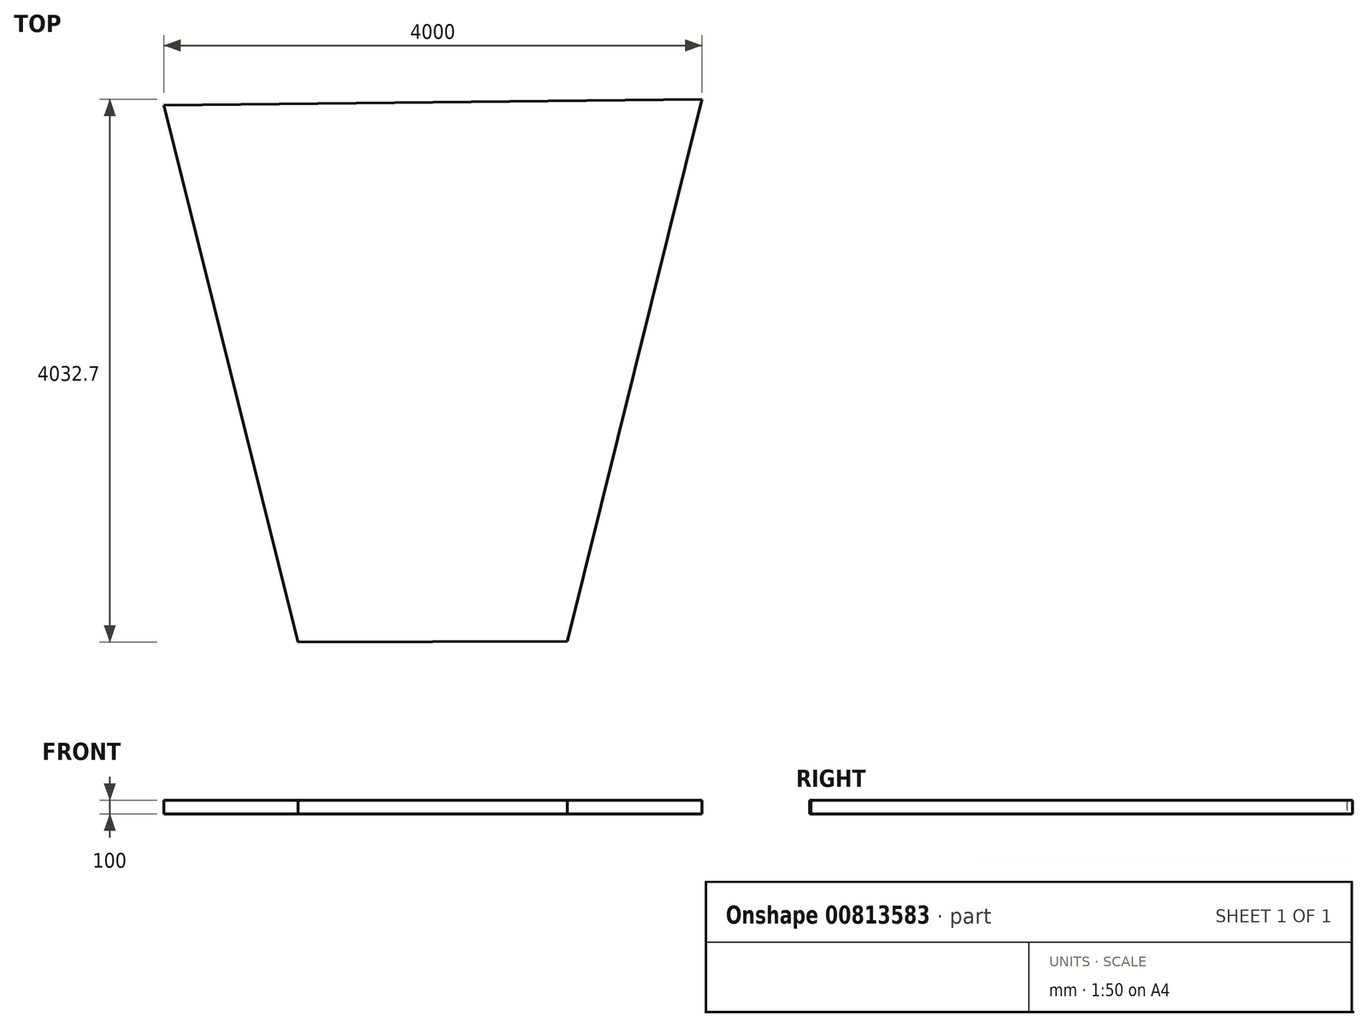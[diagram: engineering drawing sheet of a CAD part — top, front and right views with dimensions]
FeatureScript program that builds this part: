
annotation { "Feature Type Name" : "Feature", "Feature Type Description" : "" }
export const myFeature = defineFeature(function(context is Context, id is Id, definition is map)
    precondition{}
    {
        {
            var Q0;
            Q0=qCreatedBy(makeId("Top.planeOp"),FACE);
            var sketch = newSketch(context, id + "F0", { "sketchPlane" : qUnion([Q0])});
            skLineSegment(sketch, "E0", {"start": v(-1002, -940.82) * mm, "end": v(-2000, 3048.63) * mm});
            skLineSegment(sketch, "E1", {"start": v(998, -932.73) * mm, "end": v(2000, 3091.88) * mm});
            skLineSegment(sketch, "E2", {"start": v(-2000, 3048.63) * mm, "end": v(2000, 3091.88) * mm});
            skLineSegment(sketch, "E3", {"start": v(998, -932.73) * mm, "end": v(-1002, -940.82) * mm});
            skSolve(sketch);
        }
        {
            var Q0;
            Q0=makeQuery(id+"F0.imprint","IMPRINT",FACE,{"disambiguationData":[TD([[makeQuery(id+"F0.imprint","IMPRINT",EDGE,{"derivedFrom":sQuery(id+"F0.wireOp",EDGE,"E0")}),-1.0]])]});
            extrude(context, id + "F1", {"entities" : qUnion([Q0]), "depth" : 100 * mm, "offsetDistance" : 25 * mm});
        }
    });
